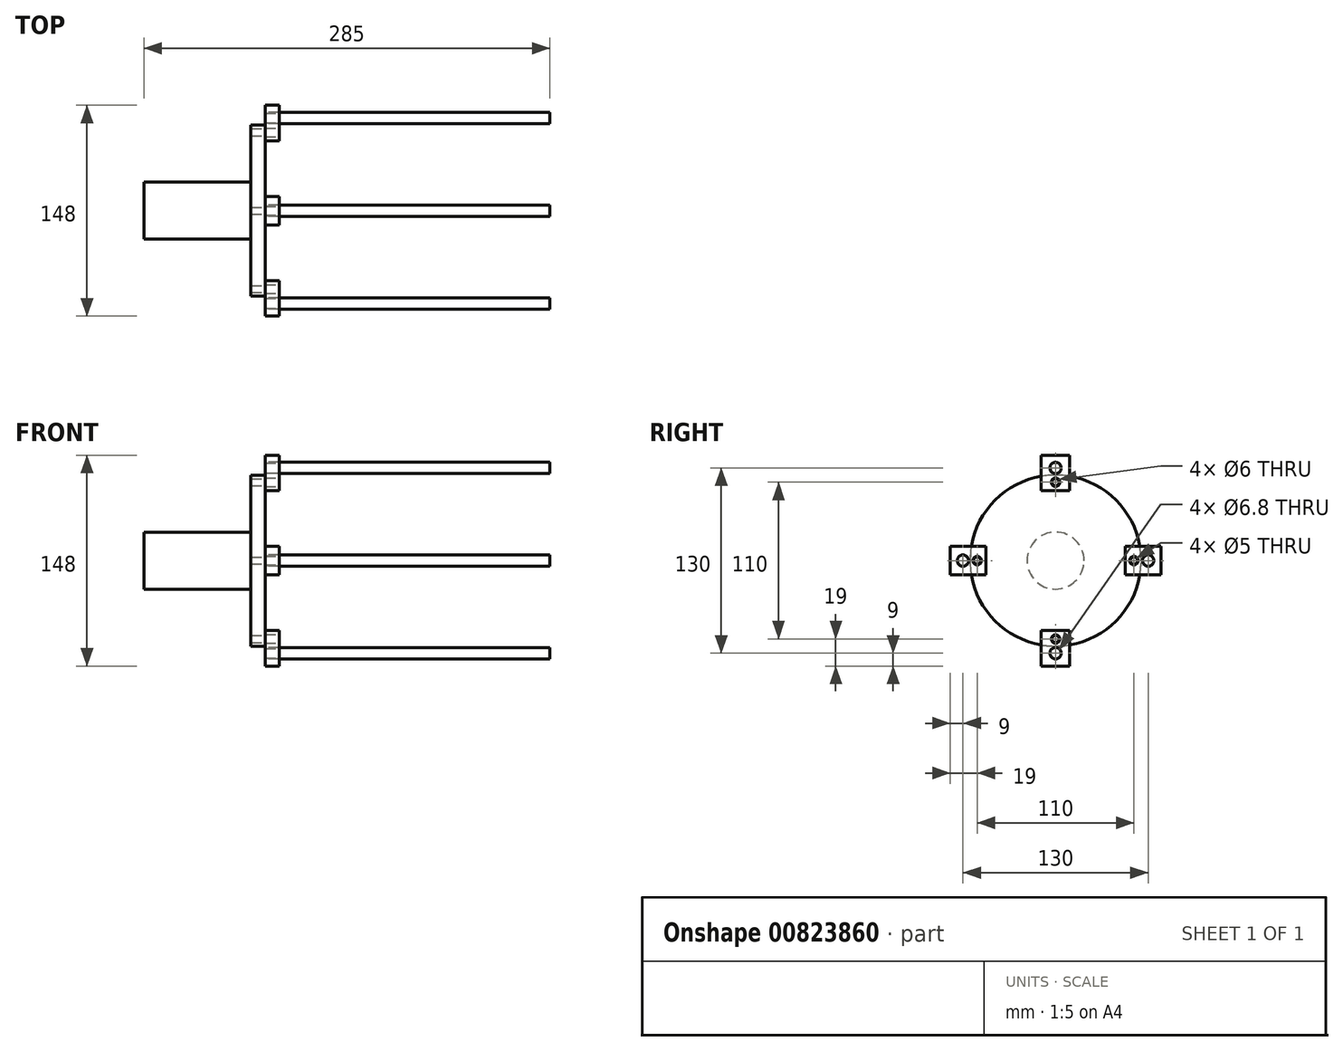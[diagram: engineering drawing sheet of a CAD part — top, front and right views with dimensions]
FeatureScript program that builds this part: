
annotation { "Feature Type Name" : "Feature", "Feature Type Description" : "" }
export const myFeature = defineFeature(function(context is Context, id is Id, definition is map)
    precondition{}
    {
        {
            var Q0;
            Q0=qCreatedBy(makeId("Front.planeOp"),FACE);
            var sketch = newSketch(context, id + "F0", { "sketchPlane" : qUnion([Q0])});
            skLineSegment(sketch, "E0", {"start": v(0, 0) * mm, "end": v(0, 20) * mm});
            skLineSegment(sketch, "E1", {"start": v(0, 20) * mm, "end": v(75, 20) * mm});
            skLineSegment(sketch, "E2", {"start": v(75, 20) * mm, "end": v(75, 60) * mm});
            skLineSegment(sketch, "E3", {"start": v(75, 60) * mm, "end": v(85, 60) * mm});
            skLineSegment(sketch, "E4", {"start": v(85, 60) * mm, "end": v(85, 0) * mm});
            skLineSegment(sketch, "E5", {"start": v(85, 0) * mm, "end": v(0, 0) * mm});
            skSolve(sketch);
        }
        {
            var Q0;
            Q0 = qSketchRegion(id + "F0", true);
            var Q1;
            Q1=sQuery(id+"F0.wireOp",EDGE,"E5");
            revolve(context, id + "F1", {"surfaceOperationType" : NewSurfaceOperationType.NEW, "entities" : qUnion([Q0]), "axis" : qUnion([Q1]), "revolveType" : RevolveType.FULL});
        }
        {
            var Q0;
            Q0=makeQuery(id+"F1.opRevolve","SWEPT_FACE",FACE,{"disambiguationData":[OSD([sQuery(id+"F0.wireOp",EDGE,"E4")])]});
            var sketch = newSketch(context, id + "F2", { "sketchPlane" : qUnion([Q0])});
            skPoint(sketch, "E6", {"position": v(0, 55) * mm});
            skPoint(sketch, "E7.1.0", {"position": v(-55, 0) * mm});
            skPoint(sketch, "E7.2.0", {"position": v(0, -55) * mm});
            skPoint(sketch, "E7.3.0", {"position": v(55, 0) * mm});
            skPoint(sketch, "E7.center", {"position": v(0, 0) * mm});
            skSolve(sketch);
        }
        {
            var Q0;
            Q0=sQuery(id+"F2.wireOp",VERTEX,"E6");
            var Q1;
            Q1=sQuery(id+"F2.wireOp",VERTEX,"E7.3.0");
            var Q2;
            Q2=sQuery(id+"F2.wireOp",VERTEX,"E7.2.0");
            var Q3;
            Q3=sQuery(id+"F2.wireOp",VERTEX,"E7.1.0");
            var Q4;
            Q4=makeQuery(id+"F1.opRevolve","SWEPT_BODY",BODY,{"disambiguationData":[OSD([sQuery(id+"F0.wireOp",EDGE,"E0"),sQuery(id+"F0.wireOp",EDGE,"E1"),sQuery(id+"F0.wireOp",EDGE,"E2"),sQuery(id+"F0.wireOp",EDGE,"E3"),sQuery(id+"F0.wireOp",EDGE,"E4"),sQuery(id+"F0.wireOp",EDGE,"E5")])]});
            hole(context, id + "F3", {"style" : HoleStyle.SIMPLE, "endStyle" : HoleEndStyle.THROUGH, "standardTappedOrClearance" : lookupTablePath({ "standard" : "ISO", "engagement" : "75%", "pitch" : "1 mm", "size" : "M6", "type" : "Tapped" }), "standardBlindInLast" : lookupTablePath({ "standard" : "ISO", "engagement" : "75%", "pitch" : "1 mm", "size" : "M6", "type" : "Tapped" }), "holeDiameter" : 5 * mm, "majorDiameter" : 6 * mm, "showTappedDepth" : true, "isTappedThrough" : true, "tappedDepth" : 22 * mm, "tapClearance" : 3, "startFromSketch" : true, "locations" : qUnion([Q0, Q1, Q2, Q3]), "scope" : qUnion([Q4])});
        }
        {
            var Q0;
            Q0=makeQuery(id+"F1.opRevolve","SWEPT_FACE",FACE,{"disambiguationData":[OSD([sQuery(id+"F0.wireOp",EDGE,"E4")])]});
            var sketch = newSketch(context, id + "F4", { "sketchPlane" : qUnion([Q0])});
            skLineSegment(sketch, "E8.bottom", {"start": v(10, 49) * mm, "end": v(-10, 49) * mm});
            skLineSegment(sketch, "E8.top", {"start": v(10, 74) * mm, "end": v(-10, 74) * mm});
            skLineSegment(sketch, "E8.left", {"start": v(10, 49) * mm, "end": v(10, 74) * mm});
            skLineSegment(sketch, "E8.right", {"start": v(-10, 49) * mm, "end": v(-10, 74) * mm});
            skPoint(sketch, "E8.middle", {"position": v(0, 61.5) * mm});
            skLineSegment(sketch, "E9", {"start": v(-10, 55) * mm, "end": v(10, 55) * mm, "construction": true});
            skLineSegment(sketch, "E10", {"start": v(0, 55) * mm, "end": v(0, 49) * mm, "construction": true});
            skSolve(sketch);
        }
        {
            var Q0;
            Q0 = qSketchRegion(id + "F4", true);
            extrude(context, id + "F5", {"entities" : qUnion([Q0]), "depth" : 10 * mm, "offsetDistance" : 25 * mm});
        }
        {
            var Q0;
            Q0=makeQuery(id+"F5.opExtrude","CAP_FACE",FACE,{"disambiguationData":[OSD([sQuery(id+"F4.wireOp",EDGE,"E8.bottom"),sQuery(id+"F4.wireOp",EDGE,"E8.top"),sQuery(id+"F4.wireOp",EDGE,"E8.left"),sQuery(id+"F4.wireOp",EDGE,"E8.right")])],"isStart":false});
            var sketch = newSketch(context, id + "F6", { "sketchPlane" : qUnion([Q0])});
            skPoint(sketch, "E11", {"position": v(0, 55) * mm});
            skSolve(sketch);
        }
        {
            var Q0;
            Q0=sQuery(id+"F6.wireOp",VERTEX,"E11");
            var Q1;
            Q1=makeQuery(id+"F5.opExtrude","SWEPT_BODY",BODY,{"disambiguationData":[OSD([sQuery(id+"F4.wireOp",EDGE,"E8.bottom"),sQuery(id+"F4.wireOp",EDGE,"E8.top"),sQuery(id+"F4.wireOp",EDGE,"E8.left"),sQuery(id+"F4.wireOp",EDGE,"E8.right")])]});
            hole(context, id + "F7", {"style" : HoleStyle.SIMPLE, "endStyle" : HoleEndStyle.THROUGH, "standardTappedOrClearance" : lookupTablePath({ "standard" : "ISO", "size" : "6", "type" : "Drilled" }), "standardBlindInLast" : lookupTablePath({ "standard" : "ISO", "size" : "6", "type" : "Drilled" }), "holeDiameter" : 6 * mm, "majorDiameter" : 6 * mm, "isTappedThrough" : true, "tappedDepth" : 22 * mm, "tapClearance" : 3, "startFromSketch" : true, "locations" : qUnion([Q0]), "scope" : qUnion([Q1])});
        }
        {
            var Q0;
            Q0=makeQuery(id+"F5.opExtrude","CAP_FACE",FACE,{"disambiguationData":[OSD([sQuery(id+"F4.wireOp",EDGE,"E8.bottom"),sQuery(id+"F4.wireOp",EDGE,"E8.top"),sQuery(id+"F4.wireOp",EDGE,"E8.left"),sQuery(id+"F4.wireOp",EDGE,"E8.right")])],"isStart":false});
            var sketch = newSketch(context, id + "F8", { "sketchPlane" : qUnion([Q0])});
            skPoint(sketch, "E12", {"position": v(0, 65) * mm});
            skSolve(sketch);
        }
        {
            var Q0;
            Q0=sQuery(id+"F8.wireOp",VERTEX,"E12");
            var Q1;
            Q1=makeQuery(id+"F5.opExtrude","SWEPT_BODY",BODY,{"disambiguationData":[OSD([sQuery(id+"F4.wireOp",EDGE,"E8.bottom"),sQuery(id+"F4.wireOp",EDGE,"E8.top"),sQuery(id+"F4.wireOp",EDGE,"E8.left"),sQuery(id+"F4.wireOp",EDGE,"E8.right")])]});
            hole(context, id + "F9", {"style" : HoleStyle.SIMPLE, "endStyle" : HoleEndStyle.THROUGH, "standardTappedOrClearance" : lookupTablePath({ "standard" : "ISO", "engagement" : "75%", "pitch" : "1.25 mm", "size" : "M8", "type" : "Tapped" }), "standardBlindInLast" : lookupTablePath({ "standard" : "ISO", "engagement" : "75%", "pitch" : "1.25 mm", "size" : "M8", "type" : "Tapped" }), "holeDiameter" : 6.8 * mm, "majorDiameter" : 8 * mm, "showTappedDepth" : true, "isTappedThrough" : true, "tappedDepth" : 22 * mm, "tapClearance" : 3, "startFromSketch" : true, "locations" : qUnion([Q0]), "scope" : qUnion([Q1])});
        }
        {
            var Q0;
            Q0=makeQuery(id+"F5.opExtrude","CAP_FACE",FACE,{"disambiguationData":[OSD([sQuery(id+"F4.wireOp",EDGE,"E8.bottom"),sQuery(id+"F4.wireOp",EDGE,"E8.top"),sQuery(id+"F4.wireOp",EDGE,"E8.left"),sQuery(id+"F4.wireOp",EDGE,"E8.right")])],"isStart":true});
            var sketch = newSketch(context, id + "F10", { "sketchPlane" : qUnion([Q0])});
            skCircle(sketch, "E13", {"center": v(0, 65) * mm, "radius": 4 * mm});
            skSolve(sketch);
        }
        {
            var Q0;
            Q0 = qSketchRegion(id + "F10", true);
            extrude(context, id + "F11", {"entities" : qUnion([Q0]), "oppositeDirection" : true, "depth" : 200 * mm, "offsetDistance" : 25 * mm});
        }
        {
            var Q0;
            Q0=makeQuery(id+"F5.opExtrude","SWEPT_BODY",BODY,{"disambiguationData":[OSD([sQuery(id+"F4.wireOp",EDGE,"E8.bottom"),sQuery(id+"F4.wireOp",EDGE,"E8.top"),sQuery(id+"F4.wireOp",EDGE,"E8.left"),sQuery(id+"F4.wireOp",EDGE,"E8.right")])]});
            var Q1;
            Q1=makeQuery(id+"F11.opExtrude","SWEPT_BODY",BODY,{"disambiguationData":[OSD([sQuery(id+"F10.wireOp",EDGE,"E13")])]});
            var Q2;
            Q2=makeQuery(id+"F1.opRevolve","SWEPT_EDGE",EDGE,{"disambiguationData":[OSD([sQuery(id+"F0.wireOp",EDGE,"E3"),sQuery(id+"F0.wireOp",EDGE,"E4")])]});
            circularPattern(context, id + "F12", {"entities" : qUnion([Q0, Q1]), "axis" : qUnion([Q2]), "angle" : 360 * degree, "instanceCount" : 4, "equalSpace" : true});
        }
    });
